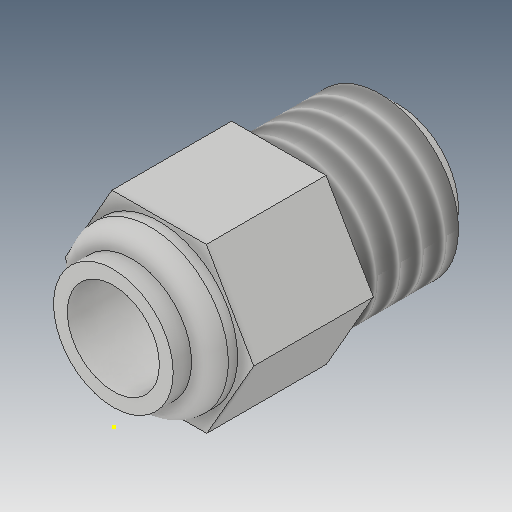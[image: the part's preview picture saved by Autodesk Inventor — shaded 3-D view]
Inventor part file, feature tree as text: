
AUTODESK INVENTOR PART (.ipt)
format: ipt  version: 2017 (Build 210142000, 142)  size: 192,512 bytes
history: native  units: mm
features: sketch x6, extrude x5, other x3, thread x1, fillet x1, chamfer x1, reference x1
ambient origin geometry x8: Origin, YZ Plane, XZ Plane, XY Plane, X Axis, Y Axis, Z Axis, Center Point
bodies: Solid1 (feature_tree)
feature tree (18):
  extrude  "Extrusion1"  Depth=10.0mm TaperAngle=0.0deg
  thread  "Thread1"  [1 undecoded]
  extrude  "Extrusion2"  Depth=1.0mm
  extrude  "Extrusion3"  Depth=1.0mm
  fillet  "Fillet1"  Radius=1.0mm
  extrude  "Extrusion4"  [1 undecoded]
  sketch  "Sketch5"
  extrude  "Extrusion5"  [1 undecoded]
  chamfer  "Chamfer1"  [1 undecoded]
  sketch  "Sketch1"  dims[d0=6.5mm d1=0.0mm d2=10.0mm d3=0.0mm d4=6.5mm d5=0.0mm]
  reference  "Reference1"
  sketch  "Sketch2"  dims[d6=1.5mm d7=0.0mm d8=1.0mm]
  sketch  "Sketch3"  dims[d9=1.0mm d10=0.0mm d11=5.0mm d12=1.0mm d13=0.0mm]
  sketch  "Sketch4"  dims[d14=1.0mm d15=2.0mm d16=45.0deg]
  sketch  "Sketch6"
  other  "<userpath>\OneDrive\Inventor\Beast 3D Printer\Hotend Mount Assembly.iam"
  other  "Hotend Mount Assembly.iam"
  other  "pshfit-mount-acrylic:1"
note: 4 required parameter values undecoded (feature->parameter linkage not recoverable at this tier; creation-order binding heuristic only, values carry confidence <= 0.55)
